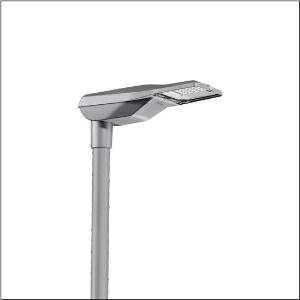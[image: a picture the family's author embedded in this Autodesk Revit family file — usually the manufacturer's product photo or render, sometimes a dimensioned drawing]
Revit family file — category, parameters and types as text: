
# Revit family: streetlight_sl_21_iq_micro___st1_0a_5xe1d21d08cb_1078
name_source: partatom
category: Lighting Fixtures
units: mm (PartAtom-declared; Revit-internal decimal feet)

## family parameters
Cut with Voids When Loaded = No
Host = Face
Light Source = No
Part Type = Normal
Room Calculation Point = No
Round Connector Dimension = Use Diameter
Shared = No

## types (1)
- --- (1 x LED, 2380 lm, 19.4 W, 2200K)
    Apparent Load = 19 VA
    CIE Flux Codes = 37 72 97 100 100
    Color Rendering = 70
    Color Temperature = 2200K
    Default Elevation = 1800 mm
    Description = Streetlight SL 21 iQ micro, mast luminaire, primary light control with lens, of PMMA, primary optical cover: cover, of toughened safety glass, transparent, light distribution: ST1.0a, light emission: direct distribution, primary light characteristic: asymmetric, installation type: post-top, side-entry, LED, High Power LED, rated luminous flux: 2.380lm, luminous efficacy: 123lm/W, light colour: 722, colour temperature: 2200K, control: Auto-Match, Temp-Guard, Lumen-Switch, Night-Set, Smart-Wire, Light-Fading, Desk-Remote (wireless, voltage-free reading and setting of iQ features in the workshop via application-optimized NFC function/RFID function), optimised constant luminous flux control (CLO 2.0), presetting dimming linear, mains connection: 220..240V, AC, 50/60Hz, start of lifetime: 19W, end of service life: 20W, reduction: 10W, luminaire housing, of diecast aluminium, powder-coated, Siteco® metallic grey (DB 702S), corrosivity category C5 mid according to DIN EN ISO 12944, please order mast flange separately, inclination adjustable: 0°, 5°, 10°, 15°, sealing non-destructively replaceable, multi-level sealing system, length: 528mm, width: 235mm, height: 110mm, mast flange for spigot size: 42mm (side-entry): 5XC10008XM4, 60/48mm (side-entry/post-top): 5XC10108XM2, 76/60mm (side-entry/post-top): 5XC10108XM1, protection rating (complete): IP66, insulation class (complete): insulation class II (safety insulation), certification: CE, ENEC, ENEC+, VDE, impact resistance: IK09, permissible operating ambient temperature for outdoor applications: -40..+50°C, standard-compliant lighting for roads and squares, packaging unit: 1 piece

Light Distribution: ST1.0a
    Height = 110 mm
    Lamp = 1 x LED
    Lamp Light Flux = 2380 lm
    Lamp Power = 19.4 W
    Lamp count = 1
    Length = 528 mm
    Luminous efficacy = 123 lm/W
    Manufacturer = Siteco
    ModVariant = No
    Model = 5XE1D21D08CB
    Number of Poles = 1
    OnlyDefault = Yes
    Power Factor = 1
    Product Name = Streetlight SL 21 iQ micro | ST1.0a
    Product group = mast luminaire | pylon top
    ProductGroupID = 6100
    Protection Class = Protection class II
    Protection Degree = IP 66
    RLX_Detail_Level = 1
    RLX_Emergency_Light_Flux = 0 lm
    RLX_Emergency_Type = 0
    RLX_Emergency_Type_DB = No
    RlxData = <blob elided: 98401 chars, md5=e76a188e>
    Socket = socket
    Standby Power = 0 W
    System Light Flux = 2380 lm
    System Power = 19 W
    Type Comments = factory setting: luminous flux: 100 % | dim-lin: 254 | 387 mA
    Type Image = l_1006881.jpg
    URL = http://relux.com
    VarID = @adj_070685
    Voltage = 0 V
    Weight = 0.00 kg
    Width = 235 mm

## geometry (parser evidence)
native form markers: Blend x4, Sweep x9
no freeform markers — native parametric forms only
